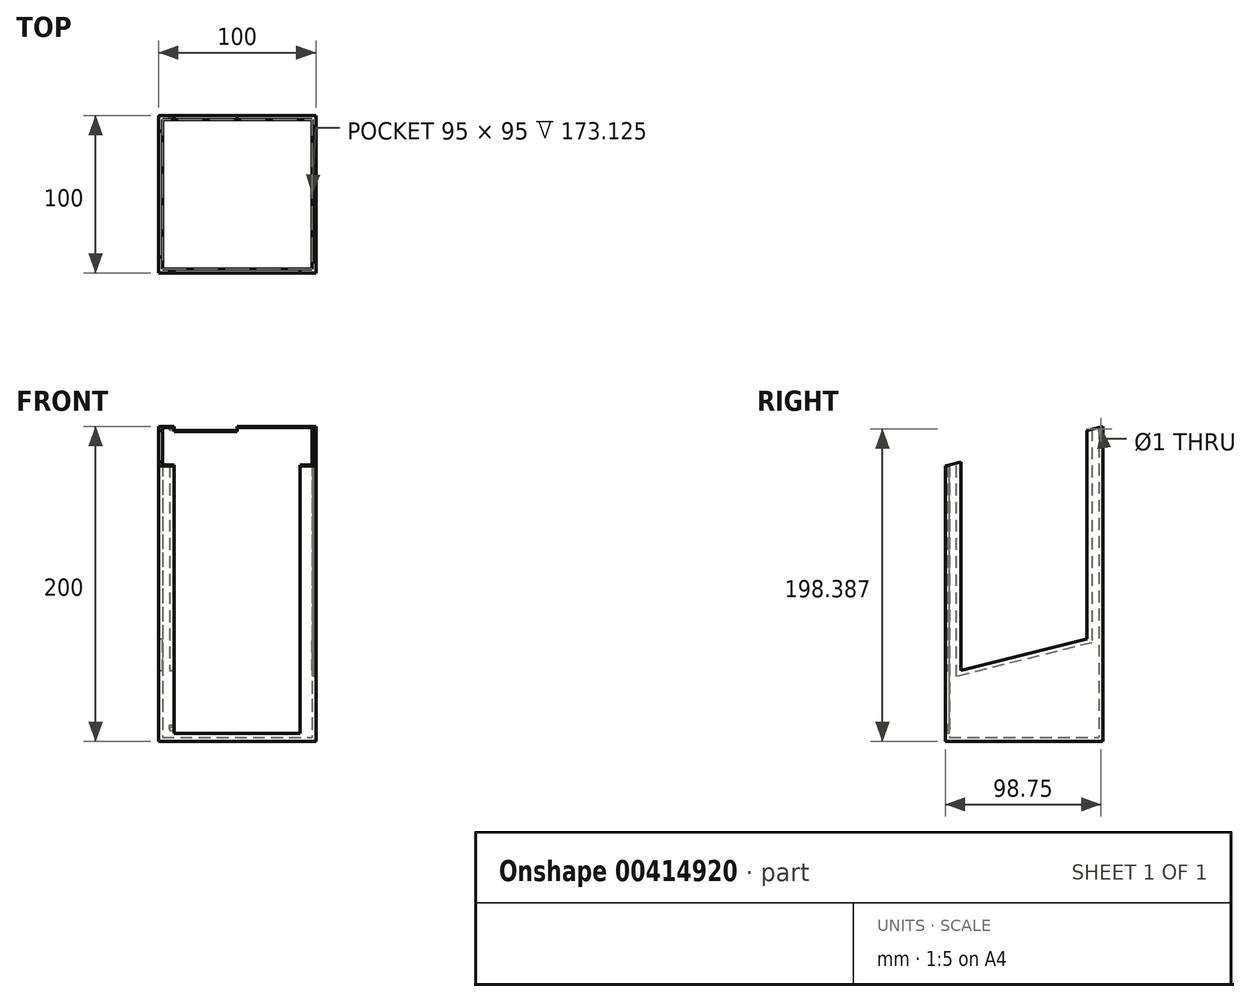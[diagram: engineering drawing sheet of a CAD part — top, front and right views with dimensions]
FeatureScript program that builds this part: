
annotation { "Feature Type Name" : "Feature", "Feature Type Description" : "" }
export const myFeature = defineFeature(function(context is Context, id is Id, definition is map)
    precondition{}
    {
        {
            var Q0;
            Q0=qCreatedBy(makeId("Right.planeOp"),FACE);
            var sketch = newSketch(context, id + "F0", { "sketchPlane" : qUnion([Q0])});
            skLineSegment(sketch, "E0.bottom", {"start": v(-50, 75.38) * mm, "end": v(50, 100.38) * mm});
            skLineSegment(sketch, "E0.top", {"start": v(-50, -99.62) * mm, "end": v(50, -99.62) * mm});
            skLineSegment(sketch, "E0.left", {"start": v(-50, 75.38) * mm, "end": v(-50, -99.62) * mm});
            skLineSegment(sketch, "E0.right", {"start": v(50, 100.38) * mm, "end": v(50, -99.62) * mm});
            skSolve(sketch);
        }
        {
            var Q0;
            Q0 = qSketchRegion(id + "F0", true);
            extrude(context, id + "F1", {"entities" : qUnion([Q0]), "endBound" : BoundingType.SYMMETRIC, "oppositeDirection" : true, "depth" : 100 * mm});
        }
        {
            var Q0;
            Q0=makeQuery(id+"F1.opExtrude","SWEPT_FACE",FACE,{"disambiguationData":[OSD([sQuery(id+"F0.wireOp",EDGE,"E0.bottom")])]});
            shell(context, id + "F2", {"entities" : qUnion([Q0]), "thickness" : 2.5 * mm});
        }
        {
            var Q0;
            Q0=makeQuery(id+"F1.opExtrude","CAP_FACE",FACE,{"disambiguationData":[OSD([sQuery(id+"F0.wireOp",EDGE,"E0.bottom"),sQuery(id+"F0.wireOp",EDGE,"E0.top"),sQuery(id+"F0.wireOp",EDGE,"E0.left"),sQuery(id+"F0.wireOp",EDGE,"E0.right")])],"isStart":true});
            var sketch = newSketch(context, id + "F3", { "sketchPlane" : qUnion([Q0])});
            skLineSegment(sketch, "E1.bottom", {"start": v(-40, 77.88) * mm, "end": v(40, 97.88) * mm});
            skLineSegment(sketch, "E1.top", {"start": v(-40, -54.62) * mm, "end": v(40, -34.62) * mm});
            skLineSegment(sketch, "E1.left", {"start": v(-40, 77.88) * mm, "end": v(-40, -54.62) * mm});
            skLineSegment(sketch, "E1.right", {"start": v(40, 97.88) * mm, "end": v(40, -34.62) * mm});
            skSolve(sketch);
        }
        {
            var Q0;
            Q0 = qSketchRegion(id + "F3", true);
            extrude(context, id + "F4", {"entities" : qUnion([Q0]), "operationType" : NewBodyOperationType.REMOVE, "endBound" : BoundingType.THROUGH_ALL, "oppositeDirection" : true, "depth" : 25 * mm});
        }
        {
            var Q0;
            Q0=makeQuery(id+"F1.opExtrude","SWEPT_FACE",FACE,{"disambiguationData":[OSD([sQuery(id+"F0.wireOp",EDGE,"E0.left")])]});
            var sketch = newSketch(context, id + "F5", { "sketchPlane" : qUnion([Q0])});
            skLineSegment(sketch, "E2.bottom", {"start": v(-40, 76) * mm, "end": v(40, 76) * mm});
            skLineSegment(sketch, "E2.top", {"start": v(-40, -94.62) * mm, "end": v(40, -94.62) * mm});
            skLineSegment(sketch, "E2.left", {"start": v(-40, 76) * mm, "end": v(-40, -94.62) * mm});
            skLineSegment(sketch, "E2.right", {"start": v(40, 76) * mm, "end": v(40, -94.62) * mm});
            skSolve(sketch);
        }
        {
            var Q0;
            Q0 = qSketchRegion(id + "F5", true);
            extrude(context, id + "F6", {"entities" : qUnion([Q0]), "operationType" : NewBodyOperationType.REMOVE, "endBound" : BoundingType.UP_TO_NEXT, "oppositeDirection" : true, "depth" : 25 * mm});
        }
        {
            var Q0;
            Q0=makeQuery(id+"F6.boolean.opBoolean","COPY",FACE,{"derivedFrom":makeQuery(id+"F6.opExtrude","SWEPT_FACE",FACE,{"disambiguationData":[OSD([sQuery(id+"F5.wireOp",EDGE,"E2.left")])]})});
            var sketch = newSketch(context, id + "F7", { "sketchPlane" : qUnion([Q0])});
            skArc(sketch, "E3", {"start": v(-49.25, -92.12) * mm, "mid": v(-48.75, -92.62) * mm, "end": v(-48.25, -92.12) * mm});
            skLineSegment(sketch, "E4.0", {"start": v(-47.5, -94.62) * mm, "end": v(-47.5, 76) * mm, "construction": true});
            skLineSegment(sketch, "E5.0", {"start": v(-50, 75.38) * mm, "end": v(-50, -94.62) * mm, "construction": true});
            skLineSegment(sketch, "E6.0", {"start": v(-47.5, -94.62) * mm, "end": v(-50, -94.62) * mm, "construction": true});
            skLineSegment(sketch, "E7", {"start": v(-47.5, -92.12) * mm, "end": v(-50, -92.12) * mm, "construction": true});
            skLineSegment(sketch, "E8", {"start": v(-47.5, -89.19) * mm, "end": v(-49.05, -89.19) * mm});
            skLineSegment(sketch, "E9", {"start": v(-49.25, -89.39) * mm, "end": v(-49.25, -92.12) * mm});
            skLineSegment(sketch, "E10", {"start": v(-48.25, -92.12) * mm, "end": v(-48.25, -90.59) * mm});
            skLineSegment(sketch, "E11", {"start": v(-48.05, -90.39) * mm, "end": v(-47.5, -90.39) * mm});
            skLineSegment(sketch, "E12", {"start": v(-47.5, -89.19) * mm, "end": v(-47.5, -90.39) * mm});
            skPoint(sketch, "E13.visualSharp", {"position": v(-48.25, -90.39) * mm});
            skArc(sketch, "E13.filletArc", {"start": v(-48.05, -90.39) * mm, "mid": v(-48.2, -90.45) * mm, "end": v(-48.25, -90.59) * mm});
            skPoint(sketch, "E14.visualSharp", {"position": v(-49.25, -89.19) * mm});
            skArc(sketch, "E14.filletArc", {"start": v(-49.05, -89.19) * mm, "mid": v(-49.2, -89.25) * mm, "end": v(-49.25, -89.39) * mm});
            skSolve(sketch);
        }
        {
            var Q0;
            Q0 = qSketchRegion(id + "F7", true);
            extrude(context, id + "F8", {"entities" : qUnion([Q0]), "operationType" : NewBodyOperationType.REMOVE, "oppositeDirection" : true, "depth" : 3 * mm});
        }
        {
            var Q0;
            Q0=makeQuery(id+"F6.boolean.opBoolean","COPY",FACE,{"derivedFrom":makeQuery(id+"F6.opExtrude","SWEPT_FACE",FACE,{"disambiguationData":[OSD([sQuery(id+"F5.wireOp",EDGE,"E2.left")])]})});
            var sketch = newSketch(context, id + "F9", { "sketchPlane" : qUnion([Q0])});
            skLineSegment(sketch, "E15.bottom", {"start": v(-49.25, 75.57) * mm, "end": v(-48.25, 75.82) * mm});
            skLineSegment(sketch, "E15.left", {"start": v(-49.25, 75.57) * mm, "end": v(-49.25, -54.62) * mm});
            skLineSegment(sketch, "E15.right", {"start": v(-48.25, 75.82) * mm, "end": v(-48.25, -54.62) * mm});
            skLineSegment(sketch, "E16", {"start": v(-50, -54.62) * mm, "end": v(-47.5, -54.62) * mm, "construction": true});
            skLineSegment(sketch, "E17", {"start": v(-49.25, -54.62) * mm, "end": v(-48.75, -54.62) * mm});
            skLineSegment(sketch, "E18", {"start": v(-48.75, -54.62) * mm, "end": v(-48.25, -54.62) * mm});
            skSolve(sketch);
        }
        {
            var Q0;
            Q0=makeQuery(id+"F9.imprint","IMPRINT",FACE,{"disambiguationData":[TD([[makeQuery(id+"F9.imprint","IMPRINT",EDGE,{"derivedFrom":sQuery(id+"F9.wireOp",EDGE,"E15.bottom")}),-1.0]])]});
            extrude(context, id + "F10", {"entities" : qUnion([Q0]), "operationType" : NewBodyOperationType.REMOVE, "oppositeDirection" : true, "depth" : 3 * mm});
        }
        {
            var Q0;
            Q0=qCreatedBy(makeId("Top.planeOp"),FACE);
            var Q1;
            Q1=makeQuery(id+"F1.opExtrude","SWEPT_EDGE",EDGE,{"disambiguationData":[OSD([sQuery(id+"F0.wireOp",EDGE,"E0.bottom"),sQuery(id+"F0.wireOp",EDGE,"E0.right")])]});
            cPlane(context, id + "F11", {"entities" : qUnion([Q0, Q1]), "cplaneType" : CPlaneType.LINE_ANGLE, "offset" : 25 * mm, "angle" : 0 * degree, "width" : 150 * mm, "height" : 150 * mm});
        }
        {
            var Q0;
            Q0=qCreatedBy(id+"F11.planeOp",FACE);
            var sketch = newSketch(context, id + "F12", { "sketchPlane" : qUnion([Q0])});
            skLineSegment(sketch, "E19.top", {"start": v(48.25, -43) * mm, "end": v(49.25, -43) * mm});
            skLineSegment(sketch, "E19.left", {"start": v(48.25, -40) * mm, "end": v(48.25, -43) * mm});
            skLineSegment(sketch, "E19.right", {"start": v(49.25, -40) * mm, "end": v(49.25, -43) * mm});
            skLineSegment(sketch, "E20.0", {"start": v(47.5, -40) * mm, "end": v(50, -40) * mm, "construction": true});
            skLineSegment(sketch, "E21", {"start": v(48.25, -40) * mm, "end": v(48.75, -40) * mm});
            skLineSegment(sketch, "E22", {"start": v(48.75, -40) * mm, "end": v(49.25, -40) * mm});
            skSolve(sketch);
        }
        {
            var Q0;
            Q0=makeQuery(id+"F1.opExtrude","CAP_FACE",FACE,{"disambiguationData":[OSD([sQuery(id+"F0.wireOp",EDGE,"E0.bottom"),sQuery(id+"F0.wireOp",EDGE,"E0.top"),sQuery(id+"F0.wireOp",EDGE,"E0.left"),sQuery(id+"F0.wireOp",EDGE,"E0.right")])],"isStart":true});
            var sketch = newSketch(context, id + "F13", { "sketchPlane" : qUnion([Q0])});
            skPoint(sketch, "E23.0", {"position": v(40, 100.38) * mm});
            skLineSegment(sketch, "E24", {"start": v(40, 100.38) * mm, "end": v(40, -34.62) * mm});
            skLineSegment(sketch, "E25", {"start": v(40, -34.62) * mm, "end": v(-40, -54.62) * mm});
            skLineSegment(sketch, "E26", {"start": v(-40, -54.62) * mm, "end": v(-40, 77.88) * mm});
            skLineSegment(sketch, "E27", {"start": v(-40, 77.88) * mm, "end": v(-40, 100.38) * mm});
            skSolve(sketch);
        }
        {
            var Q0;
            Q0 = qSketchRegion(id + "F12", true);
            var Q1;
            Q1 = qConstructionFilter(qBodyType(qCreatedBy(id + "F13" ,EDGE), BodyType.WIRE), ConstructionObject.NO);
            sweep(context, id + "F14", {"operationType" : NewBodyOperationType.REMOVE, "profiles" : qUnion([Q0]), "path" : qUnion([Q1])});
        }
        {
            var Q0;
            Q0=qCreatedBy(makeId("Right.planeOp"),FACE);
            var sketch = newSketch(context, id + "F15", { "sketchPlane" : qUnion([Q0])});
            skLineSegment(sketch, "E28.bottom", {"start": v(40, 97.88) * mm, "end": v(50, 100.38) * mm});
            skLineSegment(sketch, "E28.top", {"start": v(40, 95.28) * mm, "end": v(50, 97.78) * mm});
            skLineSegment(sketch, "E28.left", {"start": v(40, 97.88) * mm, "end": v(40, 95.28) * mm});
            skLineSegment(sketch, "E28.right", {"start": v(50, 100.38) * mm, "end": v(50, 97.78) * mm});
            skSolve(sketch);
        }
        {
            var Q0;
            Q0 = qSketchRegion(id + "F15", true);
            extrude(context, id + "F16", {"entities" : qUnion([Q0]), "operationType" : NewBodyOperationType.REMOVE, "oppositeDirection" : true, "depth" : 40 * mm});
        }
        {
            var Q0;
            Q0=makeQuery(id+"F16.boolean.opBoolean","COPY",FACE,{"derivedFrom":makeQuery(id+"F16.opExtrude","CAP_FACE",FACE,{"disambiguationData":[OSD([sQuery(id+"F15.wireOp",EDGE,"E28.bottom"),sQuery(id+"F15.wireOp",EDGE,"E28.top"),sQuery(id+"F15.wireOp",EDGE,"E28.left"),sQuery(id+"F15.wireOp",EDGE,"E28.right")])],"isStart":false})});
            var sketch = newSketch(context, id + "F17", { "sketchPlane" : qUnion([Q0])});
            skLineSegment(sketch, "E29", {"start": v(48.75, 100.07) * mm, "end": v(48.75, 97.47) * mm, "construction": true});
            skLineSegment(sketch, "E30", {"start": v(47.5, 98.45) * mm, "end": v(50, 99.08) * mm, "construction": true});
            skPoint(sketch, "E31", {"position": v(48.75, 98.77) * mm});
            skSolve(sketch);
        }
        {
            var Q0;
            Q0=sQuery(id+"F17.wireOp",VERTEX,"E31");
            var Q1;
            Q1=makeQuery(id+"F1.opExtrude","SWEPT_BODY",BODY,{"disambiguationData":[OSD([sQuery(id+"F0.wireOp",EDGE,"E0.bottom"),sQuery(id+"F0.wireOp",EDGE,"E0.top"),sQuery(id+"F0.wireOp",EDGE,"E0.left"),sQuery(id+"F0.wireOp",EDGE,"E0.right")])]});
            hole(context, id + "F18", {"style" : HoleStyle.SIMPLE, "endStyle" : HoleEndStyle.BLIND, "holeDiameter" : 1 * mm, "holeDepth" : 3 * mm, "isTappedThrough" : true, "tappedDepth" : 12 * mm, "tapClearance" : 3, "locations" : qUnion([Q0]), "scope" : qUnion([Q1])});
        }
    });
